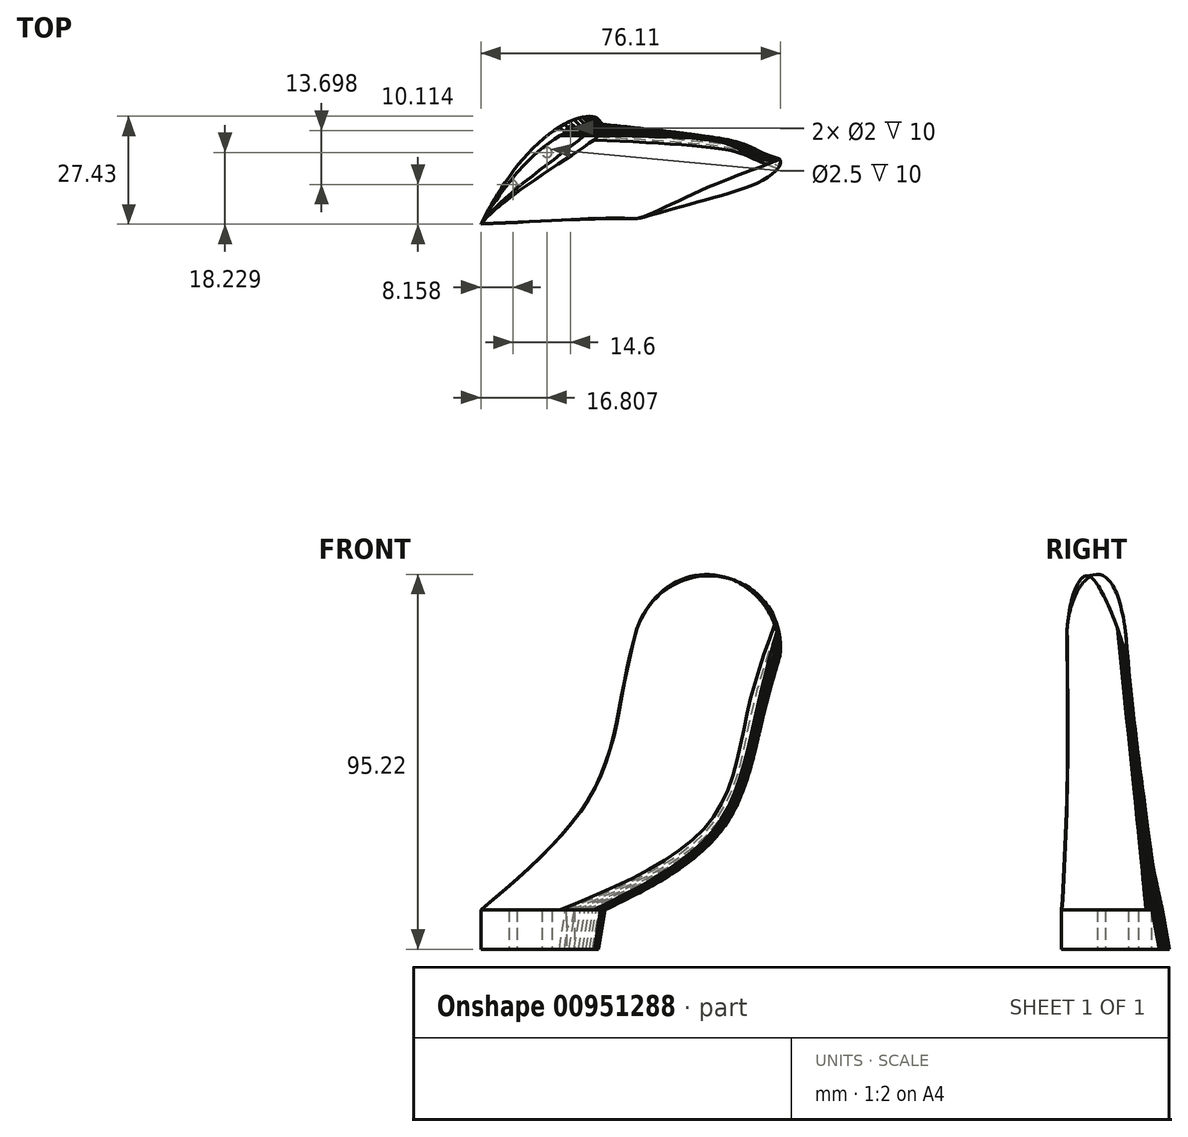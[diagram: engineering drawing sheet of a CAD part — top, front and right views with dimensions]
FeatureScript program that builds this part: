
annotation { "Feature Type Name" : "Feature", "Feature Type Description" : "" }
export const myFeature = defineFeature(function(context is Context, id is Id, definition is map)
    precondition{}
    {
        {
            var Q0;
            Q0=qCreatedBy(makeId("Top.planeOp"),FACE);
            var sketch = newSketch(context, id + "F0", { "sketchPlane" : qUnion([Q0])});
            skLineSegment(sketch, "E0", {"start": v(0, 0) * mm, "end": v(0, 60.42) * mm, "construction": true});
            skLineSegment(sketch, "E1", {"start": v(0, 0) * mm, "end": v(45.1, 0) * mm, "construction": true});
            skSolve(sketch);
        }
        {
            var Q0;
            Q0=sQuery(id+"F0.wireOp",EDGE,"E0");
            cPlane(context, id + "F1", {"entities" : qUnion([Q0]), "cplaneType" : CPlaneType.LINE_ANGLE, "offset" : 25 * mm, "angle" : 0 * degree, "width" : 150 * mm, "height" : 150 * mm});
        }
        {
            var Q0;
            Q0=sQuery(id+"F0.wireOp",EDGE,"E0");
            cPlane(context, id + "F2", {"entities" : qUnion([Q0]), "cplaneType" : CPlaneType.LINE_ANGLE, "offset" : 25 * mm, "angle" : 15 * degree, "width" : 150 * mm, "height" : 150 * mm});
        }
        {
            var Q0;
            Q0=sQuery(id+"F0.wireOp",EDGE,"E0");
            cPlane(context, id + "F3", {"entities" : qUnion([Q0]), "cplaneType" : CPlaneType.LINE_ANGLE, "offset" : 25 * mm, "angle" : 15 * degree, "width" : 150 * mm, "height" : 150 * mm});
        }
        {
            var Q0;
            Q0=sQuery(id+"F0.wireOp",EDGE,"E0");
            cPlane(context, id + "F4", {"entities" : qUnion([Q0]), "cplaneType" : CPlaneType.LINE_ANGLE, "offset" : 25 * mm, "angle" : 15 * degree, "width" : 150 * mm, "height" : 150 * mm});
        }
        {
            var Q0;
            Q0=qCreatedBy(id+"F1.planeOp",FACE);
            cPlane(context, id + "F5", {"entities" : qUnion([Q0]), "cplaneType" : CPlaneType.OFFSET, "offset" : 70 * mm, "width" : 150 * mm, "height" : 150 * mm});
        }
        {
            var Q0;
            Q0=qCreatedBy(id+"F2.planeOp",FACE);
            cPlane(context, id + "F6", {"entities" : qUnion([Q0]), "cplaneType" : CPlaneType.OFFSET, "offset" : 110 * mm, "width" : 150 * mm, "height" : 150 * mm});
        }
        {
            var Q0;
            Q0=qCreatedBy(id+"F3.planeOp",FACE);
            cPlane(context, id + "F7", {"entities" : qUnion([Q0]), "cplaneType" : CPlaneType.OFFSET, "offset" : 140 * mm, "width" : 150 * mm, "height" : 150 * mm});
        }
        {
            var Q0;
            Q0=qCreatedBy(id+"F4.planeOp",FACE);
            cPlane(context, id + "F8", {"entities" : qUnion([Q0]), "cplaneType" : CPlaneType.OFFSET, "offset" : 170 * mm, "width" : 150 * mm, "height" : 150 * mm});
        }
        {
            var Q0;
            Q0=qCreatedBy(id+"F5.planeOp",FACE);
            cPlane(context, id + "F9", {"entities" : qUnion([Q0]), "cplaneType" : CPlaneType.OFFSET, "offset" : 10 * mm, "width" : 150 * mm, "height" : 150 * mm});
        }
        {
            var Q0;
            Q0=qCreatedBy(id+"F5.planeOp",FACE);
            var sketch = newSketch(context, id + "F10", { "sketchPlane" : qUnion([Q0])});
            skLineSegment(sketch, "E2", {"start": v(-20, -2.3) * mm, "end": v(-19.93, -2.17) * mm});
            skLineSegment(sketch, "E3", {"start": v(-19.93, -2.17) * mm, "end": v(-19.75, -1.8) * mm});
            skLineSegment(sketch, "E4", {"start": v(-19.75, -1.8) * mm, "end": v(-19.47, -1.21) * mm});
            skLineSegment(sketch, "E5", {"start": v(-19.47, -1.21) * mm, "end": v(-19.1, -0.46) * mm});
            skLineSegment(sketch, "E6", {"start": v(-19.1, -0.46) * mm, "end": v(-18.6, 0.45) * mm});
            skLineSegment(sketch, "E7", {"start": v(-18.6, 0.45) * mm, "end": v(-18.02, 1.5) * mm});
            skLineSegment(sketch, "E8", {"start": v(-18.02, 1.5) * mm, "end": v(-17.33, 2.7) * mm});
            skLineSegment(sketch, "E9", {"start": v(-17.33, 2.7) * mm, "end": v(-16.57, 4) * mm});
            skLineSegment(sketch, "E10", {"start": v(-16.57, 4) * mm, "end": v(-15.72, 5.4) * mm});
            skLineSegment(sketch, "E11", {"start": v(-15.72, 5.4) * mm, "end": v(-14.8, 6.84) * mm});
            skLineSegment(sketch, "E12", {"start": v(-14.8, 6.84) * mm, "end": v(-13.83, 8.33) * mm});
            skLineSegment(sketch, "E13", {"start": v(-13.83, 8.33) * mm, "end": v(-12.78, 9.84) * mm});
            skLineSegment(sketch, "E14", {"start": v(-12.78, 9.84) * mm, "end": v(-11.68, 11.34) * mm});
            skLineSegment(sketch, "E15", {"start": v(-11.68, 11.34) * mm, "end": v(-10.51, 12.83) * mm});
            skLineSegment(sketch, "E16", {"start": v(-10.51, 12.83) * mm, "end": v(-9.3, 14.27) * mm});
            skLineSegment(sketch, "E17", {"start": v(-9.3, 14.27) * mm, "end": v(-8.03, 15.67) * mm});
            skLineSegment(sketch, "E18", {"start": v(-8.03, 15.67) * mm, "end": v(-6.73, 17) * mm});
            skLineSegment(sketch, "E19", {"start": v(-6.73, 17) * mm, "end": v(-5.4, 18.27) * mm});
            skLineSegment(sketch, "E20", {"start": v(-5.4, 18.27) * mm, "end": v(-4.07, 19.45) * mm});
            skLineSegment(sketch, "E21", {"start": v(-4.07, 19.45) * mm, "end": v(-2.73, 20.54) * mm});
            skLineSegment(sketch, "E22", {"start": v(-2.73, 20.54) * mm, "end": v(-1.4, 21.52) * mm});
            skLineSegment(sketch, "E23", {"start": v(-1.4, 21.52) * mm, "end": v(-0.09, 22.39) * mm});
            skLineSegment(sketch, "E24", {"start": v(-0.09, 22.39) * mm, "end": v(1.2, 23.14) * mm});
            skLineSegment(sketch, "E25", {"start": v(1.2, 23.14) * mm, "end": v(2.44, 23.77) * mm});
            skLineSegment(sketch, "E26", {"start": v(2.44, 23.77) * mm, "end": v(3.63, 24.27) * mm});
            skLineSegment(sketch, "E27", {"start": v(3.63, 24.27) * mm, "end": v(4.75, 24.66) * mm});
            skLineSegment(sketch, "E28", {"start": v(4.75, 24.66) * mm, "end": v(5.8, 24.93) * mm});
            skLineSegment(sketch, "E29", {"start": v(5.8, 24.93) * mm, "end": v(6.75, 25.09) * mm});
            skLineSegment(sketch, "E30", {"start": v(6.75, 25.09) * mm, "end": v(7.6, 25.13) * mm});
            skLineSegment(sketch, "E31", {"start": v(7.6, 25.13) * mm, "end": v(8.35, 25.07) * mm});
            skLineSegment(sketch, "E32", {"start": v(8.35, 25.07) * mm, "end": v(8.97, 24.92) * mm});
            skLineSegment(sketch, "E33", {"start": v(8.97, 24.92) * mm, "end": v(9.45, 24.7) * mm});
            skLineSegment(sketch, "E34", {"start": v(9.45, 24.7) * mm, "end": v(9.78, 24.4) * mm});
            skLineSegment(sketch, "E35", {"start": v(9.78, 24.4) * mm, "end": v(9.9, 24.09) * mm});
            skLineSegment(sketch, "E36", {"start": v(9.9, 24.09) * mm, "end": v(9.77, 23.69) * mm});
            skLineSegment(sketch, "E37", {"start": v(9.77, 23.69) * mm, "end": v(9.42, 23.16) * mm});
            skLineSegment(sketch, "E38", {"start": v(9.42, 23.16) * mm, "end": v(8.88, 22.53) * mm});
            skLineSegment(sketch, "E39", {"start": v(8.88, 22.53) * mm, "end": v(8.14, 21.8) * mm});
            skLineSegment(sketch, "E40", {"start": v(8.14, 21.8) * mm, "end": v(7.22, 20.95) * mm});
            skLineSegment(sketch, "E41", {"start": v(7.22, 20.95) * mm, "end": v(6.12, 20.02) * mm});
            skLineSegment(sketch, "E42", {"start": v(6.12, 20.02) * mm, "end": v(4.85, 19) * mm});
            skLineSegment(sketch, "E43", {"start": v(4.85, 19) * mm, "end": v(3.45, 17.9) * mm});
            skLineSegment(sketch, "E44", {"start": v(3.45, 17.9) * mm, "end": v(1.9, 16.72) * mm});
            skLineSegment(sketch, "E45", {"start": v(1.9, 16.72) * mm, "end": v(0.26, 15.47) * mm});
            skLineSegment(sketch, "E46", {"start": v(0.26, 15.47) * mm, "end": v(-1.47, 14.16) * mm});
            skLineSegment(sketch, "E47", {"start": v(-1.47, 14.16) * mm, "end": v(-3.26, 12.8) * mm});
            skLineSegment(sketch, "E48", {"start": v(-3.26, 12.8) * mm, "end": v(-5.1, 11.4) * mm});
            skLineSegment(sketch, "E49", {"start": v(-5.1, 11.4) * mm, "end": v(-6.93, 9.98) * mm});
            skLineSegment(sketch, "E50", {"start": v(-6.93, 9.98) * mm, "end": v(-8.76, 8.54) * mm});
            skLineSegment(sketch, "E51", {"start": v(-8.76, 8.54) * mm, "end": v(-10.53, 7.1) * mm});
            skLineSegment(sketch, "E52", {"start": v(-10.53, 7.1) * mm, "end": v(-12.22, 5.67) * mm});
            skLineSegment(sketch, "E53", {"start": v(-12.22, 5.67) * mm, "end": v(-13.8, 4.28) * mm});
            skLineSegment(sketch, "E54", {"start": v(-13.8, 4.28) * mm, "end": v(-15.23, 2.96) * mm});
            skLineSegment(sketch, "E55", {"start": v(-15.23, 2.96) * mm, "end": v(-16.5, 1.72) * mm});
            skLineSegment(sketch, "E56", {"start": v(-16.5, 1.72) * mm, "end": v(-17.6, 0.6) * mm});
            skLineSegment(sketch, "E57", {"start": v(-17.6, 0.6) * mm, "end": v(-18.5, -0.38) * mm});
            skLineSegment(sketch, "E58", {"start": v(-18.5, -0.38) * mm, "end": v(-19.18, -1.2) * mm});
            skLineSegment(sketch, "E59", {"start": v(-19.18, -1.2) * mm, "end": v(-19.65, -1.8) * mm});
            skLineSegment(sketch, "E60", {"start": v(-19.65, -1.8) * mm, "end": v(-19.91, -2.17) * mm});
            skLineSegment(sketch, "E61", {"start": v(-19.91, -2.17) * mm, "end": v(-20, -2.3) * mm});
            skSolve(sketch);
        }
        {
            var Q0;
            Q0=qCreatedBy(id+"F9.planeOp",FACE);
            var sketch = newSketch(context, id + "F11", { "sketchPlane" : qUnion([Q0])});
            skLineSegment(sketch, "E62", {"start": v(-20, -2.3) * mm, "end": v(-19.92, -2.17) * mm});
            skLineSegment(sketch, "E63", {"start": v(-19.92, -2.17) * mm, "end": v(-19.72, -1.81) * mm});
            skLineSegment(sketch, "E64", {"start": v(-19.72, -1.81) * mm, "end": v(-19.4, -1.25) * mm});
            skLineSegment(sketch, "E65", {"start": v(-19.4, -1.25) * mm, "end": v(-18.98, -0.53) * mm});
            skLineSegment(sketch, "E66", {"start": v(-18.98, -0.53) * mm, "end": v(-18.43, 0.35) * mm});
            skLineSegment(sketch, "E67", {"start": v(-18.43, 0.35) * mm, "end": v(-17.77, 1.37) * mm});
            skLineSegment(sketch, "E68", {"start": v(-17.77, 1.37) * mm, "end": v(-17.01, 2.51) * mm});
            skLineSegment(sketch, "E69", {"start": v(-17.01, 2.51) * mm, "end": v(-16.16, 3.76) * mm});
            skLineSegment(sketch, "E70", {"start": v(-16.16, 3.76) * mm, "end": v(-15.23, 5.1) * mm});
            skLineSegment(sketch, "E71", {"start": v(-15.23, 5.1) * mm, "end": v(-14.22, 6.48) * mm});
            skLineSegment(sketch, "E72", {"start": v(-14.22, 6.48) * mm, "end": v(-13.15, 7.9) * mm});
            skLineSegment(sketch, "E73", {"start": v(-13.15, 7.9) * mm, "end": v(-12, 9.34) * mm});
            skLineSegment(sketch, "E74", {"start": v(-12, 9.34) * mm, "end": v(-10.8, 10.77) * mm});
            skLineSegment(sketch, "E75", {"start": v(-10.8, 10.77) * mm, "end": v(-9.54, 12.17) * mm});
            skLineSegment(sketch, "E76", {"start": v(-9.54, 12.17) * mm, "end": v(-8.23, 13.54) * mm});
            skLineSegment(sketch, "E77", {"start": v(-8.23, 13.54) * mm, "end": v(-6.88, 14.85) * mm});
            skLineSegment(sketch, "E78", {"start": v(-6.88, 14.85) * mm, "end": v(-5.5, 16.1) * mm});
            skLineSegment(sketch, "E79", {"start": v(-5.5, 16.1) * mm, "end": v(-4.1, 17.27) * mm});
            skLineSegment(sketch, "E80", {"start": v(-4.1, 17.27) * mm, "end": v(-2.68, 18.36) * mm});
            skLineSegment(sketch, "E81", {"start": v(-2.68, 18.36) * mm, "end": v(-1.27, 19.36) * mm});
            skLineSegment(sketch, "E82", {"start": v(-1.27, 19.36) * mm, "end": v(0.12, 20.25) * mm});
            skLineSegment(sketch, "E83", {"start": v(0.12, 20.25) * mm, "end": v(1.49, 21.03) * mm});
            skLineSegment(sketch, "E84", {"start": v(1.49, 21.03) * mm, "end": v(2.81, 21.7) * mm});
            skLineSegment(sketch, "E85", {"start": v(2.81, 21.7) * mm, "end": v(4.1, 22.24) * mm});
            skLineSegment(sketch, "E86", {"start": v(4.1, 22.24) * mm, "end": v(5.31, 22.67) * mm});
            skLineSegment(sketch, "E87", {"start": v(5.31, 22.67) * mm, "end": v(6.46, 22.99) * mm});
            skLineSegment(sketch, "E88", {"start": v(6.46, 22.99) * mm, "end": v(7.52, 23.19) * mm});
            skLineSegment(sketch, "E89", {"start": v(7.52, 23.19) * mm, "end": v(8.49, 23.28) * mm});
            skLineSegment(sketch, "E90", {"start": v(8.49, 23.28) * mm, "end": v(9.34, 23.27) * mm});
            skLineSegment(sketch, "E91", {"start": v(9.34, 23.27) * mm, "end": v(10.08, 23.16) * mm});
            skLineSegment(sketch, "E92", {"start": v(10.08, 23.16) * mm, "end": v(10.68, 22.97) * mm});
            skLineSegment(sketch, "E93", {"start": v(10.68, 22.97) * mm, "end": v(11.15, 22.7) * mm});
            skLineSegment(sketch, "E94", {"start": v(11.15, 22.7) * mm, "end": v(11.46, 22.4) * mm});
            skLineSegment(sketch, "E95", {"start": v(11.46, 22.4) * mm, "end": v(11.56, 22.08) * mm});
            skLineSegment(sketch, "E96", {"start": v(11.56, 22.08) * mm, "end": v(11.4, 21.69) * mm});
            skLineSegment(sketch, "E97", {"start": v(11.4, 21.69) * mm, "end": v(11.02, 21.18) * mm});
            skLineSegment(sketch, "E98", {"start": v(11.02, 21.18) * mm, "end": v(10.44, 20.59) * mm});
            skLineSegment(sketch, "E99", {"start": v(10.44, 20.59) * mm, "end": v(9.65, 19.9) * mm});
            skLineSegment(sketch, "E100", {"start": v(9.65, 19.9) * mm, "end": v(8.68, 19.12) * mm});
            skLineSegment(sketch, "E101", {"start": v(8.68, 19.12) * mm, "end": v(7.52, 18.27) * mm});
            skLineSegment(sketch, "E102", {"start": v(7.52, 18.27) * mm, "end": v(6.2, 17.33) * mm});
            skLineSegment(sketch, "E103", {"start": v(6.2, 17.33) * mm, "end": v(4.72, 16.32) * mm});
            skLineSegment(sketch, "E104", {"start": v(4.72, 16.32) * mm, "end": v(3.1, 15.25) * mm});
            skLineSegment(sketch, "E105", {"start": v(3.1, 15.25) * mm, "end": v(1.38, 14.1) * mm});
            skLineSegment(sketch, "E106", {"start": v(1.38, 14.1) * mm, "end": v(-0.43, 12.91) * mm});
            skLineSegment(sketch, "E107", {"start": v(-0.43, 12.91) * mm, "end": v(-2.31, 11.67) * mm});
            skLineSegment(sketch, "E108", {"start": v(-2.31, 11.67) * mm, "end": v(-4.23, 10.4) * mm});
            skLineSegment(sketch, "E109", {"start": v(-4.23, 10.4) * mm, "end": v(-6.16, 9.1) * mm});
            skLineSegment(sketch, "E110", {"start": v(-6.16, 9.1) * mm, "end": v(-8.07, 7.78) * mm});
            skLineSegment(sketch, "E111", {"start": v(-8.07, 7.78) * mm, "end": v(-9.93, 6.45) * mm});
            skLineSegment(sketch, "E112", {"start": v(-9.93, 6.45) * mm, "end": v(-11.71, 5.14) * mm});
            skLineSegment(sketch, "E113", {"start": v(-11.71, 5.14) * mm, "end": v(-13.38, 3.86) * mm});
            skLineSegment(sketch, "E114", {"start": v(-13.38, 3.86) * mm, "end": v(-14.9, 2.64) * mm});
            skLineSegment(sketch, "E115", {"start": v(-14.9, 2.64) * mm, "end": v(-16.25, 1.49) * mm});
            skLineSegment(sketch, "E116", {"start": v(-16.25, 1.49) * mm, "end": v(-17.42, 0.44) * mm});
            skLineSegment(sketch, "E117", {"start": v(-17.42, 0.44) * mm, "end": v(-18.38, -0.48) * mm});
            skLineSegment(sketch, "E118", {"start": v(-18.38, -0.48) * mm, "end": v(-19.11, -1.25) * mm});
            skLineSegment(sketch, "E119", {"start": v(-19.11, -1.25) * mm, "end": v(-19.62, -1.82) * mm});
            skLineSegment(sketch, "E120", {"start": v(-19.62, -1.82) * mm, "end": v(-19.9, -2.18) * mm});
            skLineSegment(sketch, "E121", {"start": v(-19.9, -2.18) * mm, "end": v(-20, -2.3) * mm});
            skSolve(sketch);
        }
        {
            var Q0;
            Q0=qCreatedBy(id+"F6.planeOp",FACE);
            var sketch = newSketch(context, id + "F12", { "sketchPlane" : qUnion([Q0])});
            skLineSegment(sketch, "E122", {"start": v(-20, -0.93) * mm, "end": v(-19.9, -0.85) * mm});
            skLineSegment(sketch, "E123", {"start": v(-19.9, -0.85) * mm, "end": v(-19.6, -0.6) * mm});
            skLineSegment(sketch, "E124", {"start": v(-19.6, -0.6) * mm, "end": v(-19.11, -0.2) * mm});
            skLineSegment(sketch, "E125", {"start": v(-19.11, -0.2) * mm, "end": v(-18.47, 0.33) * mm});
            skLineSegment(sketch, "E126", {"start": v(-18.47, 0.33) * mm, "end": v(-17.66, 0.98) * mm});
            skLineSegment(sketch, "E127", {"start": v(-17.66, 0.98) * mm, "end": v(-16.7, 1.75) * mm});
            skLineSegment(sketch, "E128", {"start": v(-16.7, 1.75) * mm, "end": v(-15.6, 2.63) * mm});
            skLineSegment(sketch, "E129", {"start": v(-15.6, 2.63) * mm, "end": v(-14.39, 3.6) * mm});
            skLineSegment(sketch, "E130", {"start": v(-14.39, 3.6) * mm, "end": v(-13.07, 4.65) * mm});
            skLineSegment(sketch, "E131", {"start": v(-13.07, 4.65) * mm, "end": v(-11.66, 5.76) * mm});
            skLineSegment(sketch, "E132", {"start": v(-11.66, 5.76) * mm, "end": v(-10.18, 6.91) * mm});
            skLineSegment(sketch, "E133", {"start": v(-10.18, 6.91) * mm, "end": v(-8.64, 8.08) * mm});
            skLineSegment(sketch, "E134", {"start": v(-8.64, 8.08) * mm, "end": v(-7.06, 9.26) * mm});
            skLineSegment(sketch, "E135", {"start": v(-7.06, 9.26) * mm, "end": v(-5.44, 10.41) * mm});
            skLineSegment(sketch, "E136", {"start": v(-5.44, 10.41) * mm, "end": v(-3.81, 11.54) * mm});
            skLineSegment(sketch, "E137", {"start": v(-3.81, 11.54) * mm, "end": v(-2.17, 12.61) * mm});
            skLineSegment(sketch, "E138", {"start": v(-2.17, 12.61) * mm, "end": v(-0.53, 13.63) * mm});
            skLineSegment(sketch, "E139", {"start": v(-0.53, 13.63) * mm, "end": v(1.1, 14.58) * mm});
            skLineSegment(sketch, "E140", {"start": v(1.1, 14.58) * mm, "end": v(2.7, 15.47) * mm});
            skLineSegment(sketch, "E141", {"start": v(2.7, 15.47) * mm, "end": v(4.26, 16.27) * mm});
            skLineSegment(sketch, "E142", {"start": v(4.26, 16.27) * mm, "end": v(5.76, 17) * mm});
            skLineSegment(sketch, "E143", {"start": v(5.76, 17) * mm, "end": v(7.18, 17.63) * mm});
            skLineSegment(sketch, "E144", {"start": v(7.18, 17.63) * mm, "end": v(8.51, 18.16) * mm});
            skLineSegment(sketch, "E145", {"start": v(8.51, 18.16) * mm, "end": v(9.75, 18.6) * mm});
            skLineSegment(sketch, "E146", {"start": v(9.75, 18.6) * mm, "end": v(10.86, 18.93) * mm});
            skLineSegment(sketch, "E147", {"start": v(10.86, 18.93) * mm, "end": v(11.86, 19.17) * mm});
            skLineSegment(sketch, "E148", {"start": v(11.86, 19.17) * mm, "end": v(12.72, 19.3) * mm});
            skLineSegment(sketch, "E149", {"start": v(12.72, 19.3) * mm, "end": v(13.45, 19.34) * mm});
            skLineSegment(sketch, "E150", {"start": v(13.45, 19.34) * mm, "end": v(14.02, 19.29) * mm});
            skLineSegment(sketch, "E151", {"start": v(14.02, 19.29) * mm, "end": v(14.44, 19.16) * mm});
            skLineSegment(sketch, "E152", {"start": v(14.44, 19.16) * mm, "end": v(14.54, 19.1) * mm});
            skLineSegment(sketch, "E153", {"start": v(14.54, 19.1) * mm, "end": v(14.62, 19.05) * mm});
            skLineSegment(sketch, "E154", {"start": v(14.62, 19.05) * mm, "end": v(14.68, 19) * mm});
            skLineSegment(sketch, "E155", {"start": v(14.68, 19) * mm, "end": v(14.7, 18.95) * mm});
            skLineSegment(sketch, "E156", {"start": v(14.7, 18.95) * mm, "end": v(14.73, 18.91) * mm});
            skLineSegment(sketch, "E157", {"start": v(14.73, 18.91) * mm, "end": v(14.73, 18.87) * mm});
            skLineSegment(sketch, "E158", {"start": v(14.73, 18.87) * mm, "end": v(14.73, 18.82) * mm});
            skLineSegment(sketch, "E159", {"start": v(14.73, 18.82) * mm, "end": v(14.7, 18.73) * mm});
            skLineSegment(sketch, "E160", {"start": v(14.7, 18.73) * mm, "end": v(14.67, 18.63) * mm});
            skLineSegment(sketch, "E161", {"start": v(14.67, 18.63) * mm, "end": v(14.53, 18.37) * mm});
            skLineSegment(sketch, "E162", {"start": v(14.53, 18.37) * mm, "end": v(14.18, 17.93) * mm});
            skLineSegment(sketch, "E163", {"start": v(14.18, 17.93) * mm, "end": v(13.65, 17.42) * mm});
            skLineSegment(sketch, "E164", {"start": v(13.65, 17.42) * mm, "end": v(12.94, 16.85) * mm});
            skLineSegment(sketch, "E165", {"start": v(12.94, 16.85) * mm, "end": v(12.04, 16.22) * mm});
            skLineSegment(sketch, "E166", {"start": v(12.04, 16.22) * mm, "end": v(10.96, 15.54) * mm});
            skLineSegment(sketch, "E167", {"start": v(10.96, 15.54) * mm, "end": v(9.72, 14.8) * mm});
            skLineSegment(sketch, "E168", {"start": v(9.72, 14.8) * mm, "end": v(8.32, 14.02) * mm});
            skLineSegment(sketch, "E169", {"start": v(8.32, 14.02) * mm, "end": v(6.77, 13.18) * mm});
            skLineSegment(sketch, "E170", {"start": v(6.77, 13.18) * mm, "end": v(5.1, 12.3) * mm});
            skLineSegment(sketch, "E171", {"start": v(5.1, 12.3) * mm, "end": v(3.34, 11.4) * mm});
            skLineSegment(sketch, "E172", {"start": v(3.34, 11.4) * mm, "end": v(1.5, 10.45) * mm});
            skLineSegment(sketch, "E173", {"start": v(1.5, 10.45) * mm, "end": v(-0.41, 9.48) * mm});
            skLineSegment(sketch, "E174", {"start": v(-0.41, 9.48) * mm, "end": v(-2.35, 8.5) * mm});
            skLineSegment(sketch, "E175", {"start": v(-2.35, 8.5) * mm, "end": v(-4.3, 7.5) * mm});
            skLineSegment(sketch, "E176", {"start": v(-4.3, 7.5) * mm, "end": v(-6.22, 6.52) * mm});
            skLineSegment(sketch, "E177", {"start": v(-6.22, 6.52) * mm, "end": v(-8.1, 5.55) * mm});
            skLineSegment(sketch, "E178", {"start": v(-8.1, 5.55) * mm, "end": v(-9.92, 4.61) * mm});
            skLineSegment(sketch, "E179", {"start": v(-9.92, 4.61) * mm, "end": v(-11.65, 3.71) * mm});
            skLineSegment(sketch, "E180", {"start": v(-11.65, 3.71) * mm, "end": v(-13.27, 2.86) * mm});
            skLineSegment(sketch, "E181", {"start": v(-13.27, 2.86) * mm, "end": v(-14.75, 2.06) * mm});
            skLineSegment(sketch, "E182", {"start": v(-14.75, 2.06) * mm, "end": v(-16.08, 1.34) * mm});
            skLineSegment(sketch, "E183", {"start": v(-16.08, 1.34) * mm, "end": v(-17.24, 0.7) * mm});
            skLineSegment(sketch, "E184", {"start": v(-17.24, 0.7) * mm, "end": v(-18.21, 0.14) * mm});
            skLineSegment(sketch, "E185", {"start": v(-18.21, 0.14) * mm, "end": v(-18.99, -0.3) * mm});
            skLineSegment(sketch, "E186", {"start": v(-18.99, -0.3) * mm, "end": v(-19.55, -0.64) * mm});
            skLineSegment(sketch, "E187", {"start": v(-19.55, -0.64) * mm, "end": v(-19.89, -0.86) * mm});
            skLineSegment(sketch, "E188", {"start": v(-19.89, -0.86) * mm, "end": v(-20, -0.93) * mm});
            skSolve(sketch);
        }
        {
            var Q0;
            Q0=qCreatedBy(id+"F7.planeOp",FACE);
            var sketch = newSketch(context, id + "F13", { "sketchPlane" : qUnion([Q0])});
            skLineSegment(sketch, "E189", {"start": v(-20, -0.88) * mm, "end": v(-19.9, -0.8) * mm});
            skLineSegment(sketch, "E190", {"start": v(-19.9, -0.8) * mm, "end": v(-19.6, -0.55) * mm});
            skLineSegment(sketch, "E191", {"start": v(-19.6, -0.55) * mm, "end": v(-19.16, -0.17) * mm});
            skLineSegment(sketch, "E192", {"start": v(-19.16, -0.17) * mm, "end": v(-18.56, 0.32) * mm});
            skLineSegment(sketch, "E193", {"start": v(-18.56, 0.32) * mm, "end": v(-17.79, 0.9) * mm});
            skLineSegment(sketch, "E194", {"start": v(-17.79, 0.9) * mm, "end": v(-16.86, 1.57) * mm});
            skLineSegment(sketch, "E195", {"start": v(-16.86, 1.57) * mm, "end": v(-15.8, 2.32) * mm});
            skLineSegment(sketch, "E196", {"start": v(-15.8, 2.32) * mm, "end": v(-14.6, 3.15) * mm});
            skLineSegment(sketch, "E197", {"start": v(-14.6, 3.15) * mm, "end": v(-13.3, 4.03) * mm});
            skLineSegment(sketch, "E198", {"start": v(-13.3, 4.03) * mm, "end": v(-11.92, 4.94) * mm});
            skLineSegment(sketch, "E199", {"start": v(-11.92, 4.94) * mm, "end": v(-10.45, 5.85) * mm});
            skLineSegment(sketch, "E200", {"start": v(-10.45, 5.85) * mm, "end": v(-8.9, 6.77) * mm});
            skLineSegment(sketch, "E201", {"start": v(-8.9, 6.77) * mm, "end": v(-7.26, 7.66) * mm});
            skLineSegment(sketch, "E202", {"start": v(-7.26, 7.66) * mm, "end": v(-5.56, 8.53) * mm});
            skLineSegment(sketch, "E203", {"start": v(-5.56, 8.53) * mm, "end": v(-3.81, 9.38) * mm});
            skLineSegment(sketch, "E204", {"start": v(-3.81, 9.38) * mm, "end": v(-2.03, 10.2) * mm});
            skLineSegment(sketch, "E205", {"start": v(-2.03, 10.2) * mm, "end": v(-0.24, 11) * mm});
            skLineSegment(sketch, "E206", {"start": v(-0.24, 11) * mm, "end": v(1.55, 11.74) * mm});
            skLineSegment(sketch, "E207", {"start": v(1.55, 11.74) * mm, "end": v(3.3, 12.44) * mm});
            skLineSegment(sketch, "E208", {"start": v(3.3, 12.44) * mm, "end": v(5.03, 13.08) * mm});
            skLineSegment(sketch, "E209", {"start": v(5.03, 13.08) * mm, "end": v(6.68, 13.67) * mm});
            skLineSegment(sketch, "E210", {"start": v(6.68, 13.67) * mm, "end": v(8.26, 14.19) * mm});
            skLineSegment(sketch, "E211", {"start": v(8.26, 14.19) * mm, "end": v(9.73, 14.63) * mm});
            skLineSegment(sketch, "E212", {"start": v(9.73, 14.63) * mm, "end": v(11.1, 15.01) * mm});
            skLineSegment(sketch, "E213", {"start": v(11.1, 15.01) * mm, "end": v(12.34, 15.31) * mm});
            skLineSegment(sketch, "E214", {"start": v(12.34, 15.31) * mm, "end": v(13.43, 15.54) * mm});
            skLineSegment(sketch, "E215", {"start": v(13.43, 15.54) * mm, "end": v(14.38, 15.7) * mm});
            skLineSegment(sketch, "E216", {"start": v(14.38, 15.7) * mm, "end": v(15.15, 15.76) * mm});
            skLineSegment(sketch, "E217", {"start": v(15.15, 15.76) * mm, "end": v(15.76, 15.77) * mm});
            skLineSegment(sketch, "E218", {"start": v(15.76, 15.77) * mm, "end": v(16.2, 15.7) * mm});
            skLineSegment(sketch, "E219", {"start": v(16.2, 15.7) * mm, "end": v(16.32, 15.65) * mm});
            skLineSegment(sketch, "E220", {"start": v(16.32, 15.65) * mm, "end": v(16.39, 15.62) * mm});
            skLineSegment(sketch, "E221", {"start": v(16.39, 15.62) * mm, "end": v(16.44, 15.58) * mm});
            skLineSegment(sketch, "E222", {"start": v(16.44, 15.58) * mm, "end": v(16.46, 15.55) * mm});
            skLineSegment(sketch, "E223", {"start": v(16.46, 15.55) * mm, "end": v(16.48, 15.53) * mm});
            skLineSegment(sketch, "E224", {"start": v(16.48, 15.53) * mm, "end": v(16.48, 15.5) * mm});
            skLineSegment(sketch, "E225", {"start": v(16.48, 15.5) * mm, "end": v(16.47, 15.46) * mm});
            skLineSegment(sketch, "E226", {"start": v(16.47, 15.46) * mm, "end": v(16.43, 15.4) * mm});
            skLineSegment(sketch, "E227", {"start": v(16.43, 15.4) * mm, "end": v(16.38, 15.33) * mm});
            skLineSegment(sketch, "E228", {"start": v(16.38, 15.33) * mm, "end": v(16.24, 15.16) * mm});
            skLineSegment(sketch, "E229", {"start": v(16.24, 15.16) * mm, "end": v(15.83, 14.81) * mm});
            skLineSegment(sketch, "E230", {"start": v(15.83, 14.81) * mm, "end": v(15.23, 14.4) * mm});
            skLineSegment(sketch, "E231", {"start": v(15.23, 14.4) * mm, "end": v(14.44, 13.92) * mm});
            skLineSegment(sketch, "E232", {"start": v(14.44, 13.92) * mm, "end": v(13.48, 13.37) * mm});
            skLineSegment(sketch, "E233", {"start": v(13.48, 13.37) * mm, "end": v(12.34, 12.77) * mm});
            skLineSegment(sketch, "E234", {"start": v(12.34, 12.77) * mm, "end": v(11.05, 12.11) * mm});
            skLineSegment(sketch, "E235", {"start": v(11.05, 12.11) * mm, "end": v(9.63, 11.42) * mm});
            skLineSegment(sketch, "E236", {"start": v(9.63, 11.42) * mm, "end": v(8.08, 10.7) * mm});
            skLineSegment(sketch, "E237", {"start": v(8.08, 10.7) * mm, "end": v(6.43, 9.96) * mm});
            skLineSegment(sketch, "E238", {"start": v(6.43, 9.96) * mm, "end": v(4.68, 9.22) * mm});
            skLineSegment(sketch, "E239", {"start": v(4.68, 9.22) * mm, "end": v(2.84, 8.5) * mm});
            skLineSegment(sketch, "E240", {"start": v(2.84, 8.5) * mm, "end": v(0.93, 7.77) * mm});
            skLineSegment(sketch, "E241", {"start": v(0.93, 7.77) * mm, "end": v(-1.06, 7.04) * mm});
            skLineSegment(sketch, "E242", {"start": v(-1.06, 7.04) * mm, "end": v(-3.08, 6.32) * mm});
            skLineSegment(sketch, "E243", {"start": v(-3.08, 6.32) * mm, "end": v(-5.1, 5.58) * mm});
            skLineSegment(sketch, "E244", {"start": v(-5.1, 5.58) * mm, "end": v(-7.12, 4.84) * mm});
            skLineSegment(sketch, "E245", {"start": v(-7.12, 4.84) * mm, "end": v(-9.08, 4.1) * mm});
            skLineSegment(sketch, "E246", {"start": v(-9.08, 4.1) * mm, "end": v(-10.95, 3.37) * mm});
            skLineSegment(sketch, "E247", {"start": v(-10.95, 3.37) * mm, "end": v(-12.71, 2.65) * mm});
            skLineSegment(sketch, "E248", {"start": v(-12.71, 2.65) * mm, "end": v(-14.33, 1.96) * mm});
            skLineSegment(sketch, "E249", {"start": v(-14.33, 1.96) * mm, "end": v(-15.79, 1.3) * mm});
            skLineSegment(sketch, "E250", {"start": v(-15.79, 1.3) * mm, "end": v(-17.05, 0.71) * mm});
            skLineSegment(sketch, "E251", {"start": v(-17.05, 0.71) * mm, "end": v(-18.1, 0.19) * mm});
            skLineSegment(sketch, "E252", {"start": v(-18.1, 0.19) * mm, "end": v(-18.94, -0.26) * mm});
            skLineSegment(sketch, "E253", {"start": v(-18.94, -0.26) * mm, "end": v(-19.53, -0.6) * mm});
            skLineSegment(sketch, "E254", {"start": v(-19.53, -0.6) * mm, "end": v(-19.88, -0.8) * mm});
            skLineSegment(sketch, "E255", {"start": v(-19.88, -0.8) * mm, "end": v(-20, -0.88) * mm});
            skSolve(sketch);
        }
        {
            var Q0;
            Q0=qCreatedBy(id+"F8.planeOp",FACE);
            var sketch = newSketch(context, id + "F14", { "sketchPlane" : qUnion([Q0])});
            skLineSegment(sketch, "E256", {"start": v(-20, -1.07) * mm, "end": v(-19.89, -1) * mm});
            skLineSegment(sketch, "E257", {"start": v(-19.89, -1) * mm, "end": v(-19.58, -0.75) * mm});
            skLineSegment(sketch, "E258", {"start": v(-19.58, -0.75) * mm, "end": v(-19.12, -0.38) * mm});
            skLineSegment(sketch, "E259", {"start": v(-19.12, -0.38) * mm, "end": v(-18.5, 0.08) * mm});
            skLineSegment(sketch, "E260", {"start": v(-18.5, 0.08) * mm, "end": v(-17.7, 0.62) * mm});
            skLineSegment(sketch, "E261", {"start": v(-17.7, 0.62) * mm, "end": v(-16.74, 1.25) * mm});
            skLineSegment(sketch, "E262", {"start": v(-16.74, 1.25) * mm, "end": v(-15.64, 1.95) * mm});
            skLineSegment(sketch, "E263", {"start": v(-15.64, 1.95) * mm, "end": v(-14.4, 2.72) * mm});
            skLineSegment(sketch, "E264", {"start": v(-14.4, 2.72) * mm, "end": v(-13.07, 3.53) * mm});
            skLineSegment(sketch, "E265", {"start": v(-13.07, 3.53) * mm, "end": v(-11.65, 4.37) * mm});
            skLineSegment(sketch, "E266", {"start": v(-11.65, 4.37) * mm, "end": v(-10.14, 5.2) * mm});
            skLineSegment(sketch, "E267", {"start": v(-10.14, 5.2) * mm, "end": v(-8.55, 6.02) * mm});
            skLineSegment(sketch, "E268", {"start": v(-8.55, 6.02) * mm, "end": v(-6.88, 6.82) * mm});
            skLineSegment(sketch, "E269", {"start": v(-6.88, 6.82) * mm, "end": v(-5.15, 7.58) * mm});
            skLineSegment(sketch, "E270", {"start": v(-5.15, 7.58) * mm, "end": v(-3.36, 8.32) * mm});
            skLineSegment(sketch, "E271", {"start": v(-3.36, 8.32) * mm, "end": v(-1.54, 9.02) * mm});
            skLineSegment(sketch, "E272", {"start": v(-1.54, 9.02) * mm, "end": v(0.29, 9.7) * mm});
            skLineSegment(sketch, "E273", {"start": v(0.29, 9.7) * mm, "end": v(2.11, 10.31) * mm});
            skLineSegment(sketch, "E274", {"start": v(2.11, 10.31) * mm, "end": v(3.91, 10.89) * mm});
            skLineSegment(sketch, "E275", {"start": v(3.91, 10.89) * mm, "end": v(5.67, 11.4) * mm});
            skLineSegment(sketch, "E276", {"start": v(5.67, 11.4) * mm, "end": v(7.36, 11.87) * mm});
            skLineSegment(sketch, "E277", {"start": v(7.36, 11.87) * mm, "end": v(8.97, 12.27) * mm});
            skLineSegment(sketch, "E278", {"start": v(8.97, 12.27) * mm, "end": v(10.48, 12.6) * mm});
            skLineSegment(sketch, "E279", {"start": v(10.48, 12.6) * mm, "end": v(11.88, 12.88) * mm});
            skLineSegment(sketch, "E280", {"start": v(11.88, 12.88) * mm, "end": v(13.15, 13.08) * mm});
            skLineSegment(sketch, "E281", {"start": v(13.15, 13.08) * mm, "end": v(14.27, 13.22) * mm});
            skLineSegment(sketch, "E282", {"start": v(14.27, 13.22) * mm, "end": v(15.24, 13.29) * mm});
            skLineSegment(sketch, "E283", {"start": v(15.24, 13.29) * mm, "end": v(16.05, 13.28) * mm});
            skLineSegment(sketch, "E284", {"start": v(16.05, 13.28) * mm, "end": v(16.68, 13.22) * mm});
            skLineSegment(sketch, "E285", {"start": v(16.68, 13.22) * mm, "end": v(17.14, 13.1) * mm});
            skLineSegment(sketch, "E286", {"start": v(17.14, 13.1) * mm, "end": v(17.37, 12.98) * mm});
            skLineSegment(sketch, "E287", {"start": v(17.37, 12.98) * mm, "end": v(17.44, 12.92) * mm});
            skLineSegment(sketch, "E288", {"start": v(17.44, 12.92) * mm, "end": v(17.48, 12.87) * mm});
            skLineSegment(sketch, "E289", {"start": v(17.48, 12.87) * mm, "end": v(17.5, 12.84) * mm});
            skLineSegment(sketch, "E290", {"start": v(17.5, 12.84) * mm, "end": v(17.51, 12.8) * mm});
            skLineSegment(sketch, "E291", {"start": v(17.51, 12.8) * mm, "end": v(17.5, 12.77) * mm});
            skLineSegment(sketch, "E292", {"start": v(17.5, 12.77) * mm, "end": v(17.5, 12.74) * mm});
            skLineSegment(sketch, "E293", {"start": v(17.5, 12.74) * mm, "end": v(17.45, 12.67) * mm});
            skLineSegment(sketch, "E294", {"start": v(17.45, 12.67) * mm, "end": v(17.39, 12.6) * mm});
            skLineSegment(sketch, "E295", {"start": v(17.39, 12.6) * mm, "end": v(17.32, 12.53) * mm});
            skLineSegment(sketch, "E296", {"start": v(17.32, 12.53) * mm, "end": v(16.94, 12.23) * mm});
            skLineSegment(sketch, "E297", {"start": v(16.94, 12.23) * mm, "end": v(16.35, 11.87) * mm});
            skLineSegment(sketch, "E298", {"start": v(16.35, 11.87) * mm, "end": v(15.55, 11.46) * mm});
            skLineSegment(sketch, "E299", {"start": v(15.55, 11.46) * mm, "end": v(14.57, 10.99) * mm});
            skLineSegment(sketch, "E300", {"start": v(14.57, 10.99) * mm, "end": v(13.42, 10.48) * mm});
            skLineSegment(sketch, "E301", {"start": v(13.42, 10.48) * mm, "end": v(12.1, 9.92) * mm});
            skLineSegment(sketch, "E302", {"start": v(12.1, 9.92) * mm, "end": v(10.64, 9.34) * mm});
            skLineSegment(sketch, "E303", {"start": v(10.64, 9.34) * mm, "end": v(9.06, 8.73) * mm});
            skLineSegment(sketch, "E304", {"start": v(9.06, 8.73) * mm, "end": v(7.36, 8.12) * mm});
            skLineSegment(sketch, "E305", {"start": v(7.36, 8.12) * mm, "end": v(5.56, 7.5) * mm});
            skLineSegment(sketch, "E306", {"start": v(5.56, 7.5) * mm, "end": v(3.67, 6.9) * mm});
            skLineSegment(sketch, "E307", {"start": v(3.67, 6.9) * mm, "end": v(1.7, 6.31) * mm});
            skLineSegment(sketch, "E308", {"start": v(1.7, 6.31) * mm, "end": v(-0.35, 5.72) * mm});
            skLineSegment(sketch, "E309", {"start": v(-0.35, 5.72) * mm, "end": v(-2.43, 5.13) * mm});
            skLineSegment(sketch, "E310", {"start": v(-2.43, 5.13) * mm, "end": v(-4.53, 4.52) * mm});
            skLineSegment(sketch, "E311", {"start": v(-4.53, 4.52) * mm, "end": v(-6.6, 3.91) * mm});
            skLineSegment(sketch, "E312", {"start": v(-6.6, 3.91) * mm, "end": v(-8.63, 3.3) * mm});
            skLineSegment(sketch, "E313", {"start": v(-8.63, 3.3) * mm, "end": v(-10.57, 2.68) * mm});
            skLineSegment(sketch, "E314", {"start": v(-10.57, 2.68) * mm, "end": v(-12.4, 2.07) * mm});
            skLineSegment(sketch, "E315", {"start": v(-12.4, 2.07) * mm, "end": v(-14.08, 1.47) * mm});
            skLineSegment(sketch, "E316", {"start": v(-14.08, 1.47) * mm, "end": v(-15.6, 0.9) * mm});
            skLineSegment(sketch, "E317", {"start": v(-15.6, 0.9) * mm, "end": v(-16.92, 0.38) * mm});
            skLineSegment(sketch, "E318", {"start": v(-16.92, 0.38) * mm, "end": v(-18.02, -0.1) * mm});
            skLineSegment(sketch, "E319", {"start": v(-18.02, -0.1) * mm, "end": v(-18.89, -0.5) * mm});
            skLineSegment(sketch, "E320", {"start": v(-18.89, -0.5) * mm, "end": v(-19.5, -0.8) * mm});
            skLineSegment(sketch, "E321", {"start": v(-19.5, -0.8) * mm, "end": v(-19.88, -1) * mm});
            skLineSegment(sketch, "E322", {"start": v(-19.88, -1) * mm, "end": v(-20, -1.07) * mm});
            skSolve(sketch);
        }
        {
            var Q0;
            Q0 = qSketchRegion(id + "F11", true);
            var Q1;
            Q1 = qSketchRegion(id + "F12", true);
            var Q2;
            Q2 = qSketchRegion(id + "F13", true);
            var Q3;
            Q3 = qSketchRegion(id + "F14", true);
            loft(context, id + "F15", {"sheetProfilesArray" : [{ "sheetProfileEntities" : qUnion([Q0]) }, { "sheetProfileEntities" : qUnion([Q1]) }, { "sheetProfileEntities" : qUnion([Q2]) }, { "sheetProfileEntities" : qUnion([Q3]) }]});
        }
        {
            var Q1;
            Q1 = qSketchRegion(id + "F10", true);
            var Q2;
            Q2 = qSketchRegion(id + "F11", true);
            loft(context, id + "F16", {"operationType" : NewBodyOperationType.ADD, "sheetProfilesArray" : [{ "sheetProfileEntities" : qUnion([Q1]) }, { "sheetProfileEntities" : qUnion([Q2]) }]});
        }
        {
            var Q0;
            Q0=makeQuery(id+"F14.imprint","IMPRINT",FACE,{"disambiguationData":[TD([[makeQuery(id+"F14.imprint","IMPRINT",EDGE,{"derivedFrom":sQuery(id+"F14.wireOp",EDGE,"E256")}),-1.0]])]});
            var sketch = newSketch(context, id + "F17", { "sketchPlane" : qUnion([Q0])});
            skLineSegment(sketch, "E323", {"start": v(-19.93, -1.04) * mm, "end": v(17.52, 12.87) * mm, "construction": true});
            skSolve(sketch);
        }
        {
            var Q0;
            Q0=sQuery(id+"F17.wireOp",EDGE,"E323");
            cPlane(context, id + "F18", {"entities" : qUnion([Q0]), "cplaneType" : CPlaneType.LINE_ANGLE, "offset" : 25 * mm, "angle" : 7 * degree, "width" : 150 * mm, "height" : 150 * mm});
        }
        {
            var Q0;
            Q0=qCreatedBy(id+"F18.planeOp",FACE);
            cPlane(context, id + "F19", {"entities" : qUnion([Q0]), "cplaneType" : CPlaneType.OFFSET, "offset" : 2 * mm, "oppositeDirection" : true, "width" : 150 * mm, "height" : 150 * mm});
        }
        {
            var Q0;
            Q0=qCreatedBy(id+"F19.planeOp",FACE);
            var sketch = newSketch(context, id + "F20", { "sketchPlane" : qUnion([Q0])});
            skLineSegment(sketch, "E324", {"start": v(-24.53, 150.4) * mm, "end": v(-15.24, 173.34) * mm});
            skLineSegment(sketch, "E325", {"start": v(-15.24, 173.34) * mm, "end": v(-43.95, 172.32) * mm});
            skLineSegment(sketch, "E326", {"start": v(-43.95, 172.32) * mm, "end": v(-76.48, 159.09) * mm});
            skLineSegment(sketch, "E327", {"start": v(-76.48, 159.09) * mm, "end": v(-67.72, 143.54) * mm});
            skLineSegment(sketch, "E328", {"start": v(-67.72, 143.54) * mm, "end": v(-63.1, 139.23) * mm});
            skLineSegment(sketch, "E329", {"start": v(-29.26, 167.6) * mm, "end": v(-24.53, 150.4) * mm, "construction": true});
            skLineSegment(sketch, "E330", {"start": v(-67.84, 156.42) * mm, "end": v(-63.1, 139.23) * mm, "construction": true});
            skArc(sketch, "E331", {"start": v(-24.53, 150.4) * mm, "mid": v(-48.88, 162.28) * mm, "end": v(-63.1, 139.23) * mm});
            skSolve(sketch);
        }
        {
            var Q0;
            Q0 = qSketchRegion(id + "F20", true);
            extrude(context, id + "F21", {"entities" : qUnion([Q0]), "operationType" : NewBodyOperationType.REMOVE, "endBound" : BoundingType.THROUGH_ALL, "depth" : 25 * mm, "offsetDistance" : 25 * mm});
        }
        {
            var Q0;
            Q0=makeQuery(id+"F16.opLoft","CAP_FACE",FACE,{"disambiguationData":[OSD([makeQuery(id+"F10.imprint","IMPRINT",FACE,{"disambiguationData":[TD([[makeQuery(id+"F10.imprint","IMPRINT",EDGE,{"derivedFrom":sQuery(id+"F10.wireOp",EDGE,"E2")}),-1.0]])]})])],"isStart":true});
            var sketch = newSketch(context, id + "F22", { "sketchPlane" : qUnion([Q0])});
            skLineSegment(sketch, "E332", {"start": v(8.97, -24.92) * mm, "end": v(-19.91, 2.17) * mm, "construction": true});
            skLineSegment(sketch, "E333", {"start": v(-21.56, 1.3) * mm, "end": v(7.95, -26.38) * mm});
            skCircle(sketch, "E334", {"center": v(-3.2, -15.93) * mm, "radius": 1.25 * mm});
            skCircle(sketch, "E335", {"center": v(-11.84, -7.81) * mm, "radius": 1 * mm});
            skPoint(sketch, "E335.centerSnap0", {"position": v(-9.64, -7.81) * mm});
            skCircle(sketch, "E336", {"center": v(2.76, -21.51) * mm, "radius": 1 * mm});
            skSolve(sketch);
        }
        {
            var Q0;
            Q0 = qSketchRegion(id + "F22", true);
            extrude(context, id + "F23", {"entities" : qUnion([Q0]), "operationType" : NewBodyOperationType.REMOVE, "oppositeDirection" : true, "depth" : 10 * mm, "offsetDistance" : 25 * mm});
        }
    });
